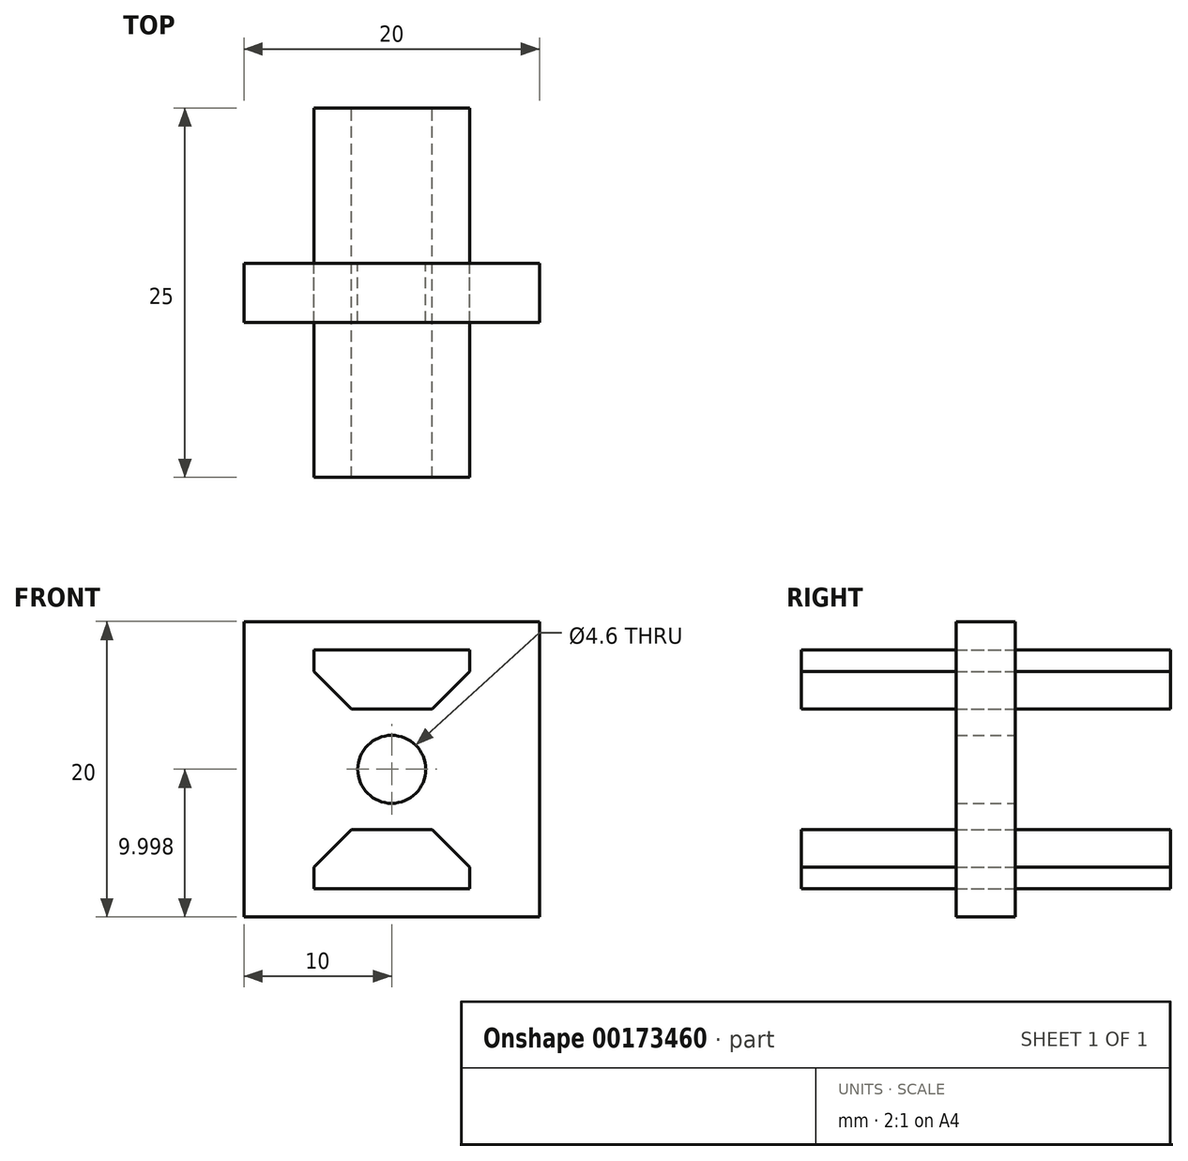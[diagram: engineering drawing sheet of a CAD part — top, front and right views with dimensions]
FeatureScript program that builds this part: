
annotation { "Feature Type Name" : "Feature", "Feature Type Description" : "" }
export const myFeature = defineFeature(function(context is Context, id is Id, definition is map)
    precondition{}
    {
        {
            var Q0;
            Q0=qCreatedBy(makeId("Front.planeOp"),FACE);
            var sketch = newSketch(context, id + "F0", { "sketchPlane" : qUnion([Q0])});
            skLineSegment(sketch, "E0.0", {"start": v(5.27, -8.38) * mm, "end": v(-5.27, -8.38) * mm});
            skLineSegment(sketch, "E1.0", {"start": v(5.27, -9.84) * mm, "end": v(5.27, -8.38) * mm});
            skLineSegment(sketch, "E2.0", {"start": v(2.73, -12.38) * mm, "end": v(5.27, -9.84) * mm});
            skLineSegment(sketch, "E3.0", {"start": v(-2.73, -12.38) * mm, "end": v(2.73, -12.38) * mm});
            skLineSegment(sketch, "E4.0", {"start": v(-5.27, -9.84) * mm, "end": v(-2.73, -12.38) * mm});
            skLineSegment(sketch, "E5.0", {"start": v(-5.27, -8.38) * mm, "end": v(-5.27, -9.84) * mm});
            skPoint(sketch, "E6.start.orphan", {"position": v(2.77, -12.47) * mm});
            skSolve(sketch);
        }
        {
            var Q0;
            Q0=qCreatedBy(makeId("Front.planeOp"),FACE);
            var sketch = newSketch(context, id + "F1", { "sketchPlane" : qUnion([Q0])});
            skLineSegment(sketch, "E7.bottom", {"start": v(-10, -6.46) * mm, "end": v(10, -6.46) * mm});
            skLineSegment(sketch, "E7.top", {"start": v(-10, -26.46) * mm, "end": v(10, -26.46) * mm});
            skLineSegment(sketch, "E7.left", {"start": v(-10, -6.46) * mm, "end": v(-10, -26.46) * mm});
            skLineSegment(sketch, "E7.right", {"start": v(10, -6.46) * mm, "end": v(10, -26.46) * mm});
            skCircle(sketch, "E8", {"center": v(0, -16.46) * mm, "radius": 2.3 * mm});
            skSolve(sketch);
        }
        {
            var Q0;
            Q0=makeQuery(id+"F1.imprint","IMPRINT",FACE,{"disambiguationData":[TD([[makeQuery(id+"F1.imprint","IMPRINT",EDGE,{"derivedFrom":sQuery(id+"F1.wireOp",EDGE,"E7.bottom")}),-1.0]])]});
            extrude(context, id + "F2", {"entities" : qUnion([Q0]), "endBound" : BoundingType.SYMMETRIC, "depth" : 4 * mm});
        }
        {
            var Q0;
            Q0=makeQuery(id+"F0.imprint","IMPRINT",FACE,{"disambiguationData":[TD([[makeQuery(id+"F0.imprint","IMPRINT",EDGE,{"derivedFrom":sQuery(id+"F0.wireOp",EDGE,"E0.0")}),1.0]])]});
            extrude(context, id + "F3", {"entities" : qUnion([Q0]), "endBound" : BoundingType.SYMMETRIC, "depth" : 25 * mm});
        }
        {
            var Q0;
            Q0=makeQuery(id+"F3.opExtrude","SWEPT_BODY",BODY,{"disambiguationData":[OSD([sQuery(id+"F0.wireOp",EDGE,"E0.0"),sQuery(id+"F0.wireOp",EDGE,"E1.0"),sQuery(id+"F0.wireOp",EDGE,"E2.0"),sQuery(id+"F0.wireOp",EDGE,"E3.0"),sQuery(id+"F0.wireOp",EDGE,"E4.0"),sQuery(id+"F0.wireOp",EDGE,"E5.0")])]});
            var Q1;
            Q1=makeQuery(id+"F2.opExtrude","SWEPT_FACE",FACE,{"disambiguationData":[OSD([sQuery(id+"F1.wireOp",EDGE,"E8")])]});
            circularPattern(context, id + "F4", {"entities" : qUnion([Q0]), "axis" : qUnion([Q1]), "angle" : 180 * degree, "instanceCount" : 2});
        }
    });
